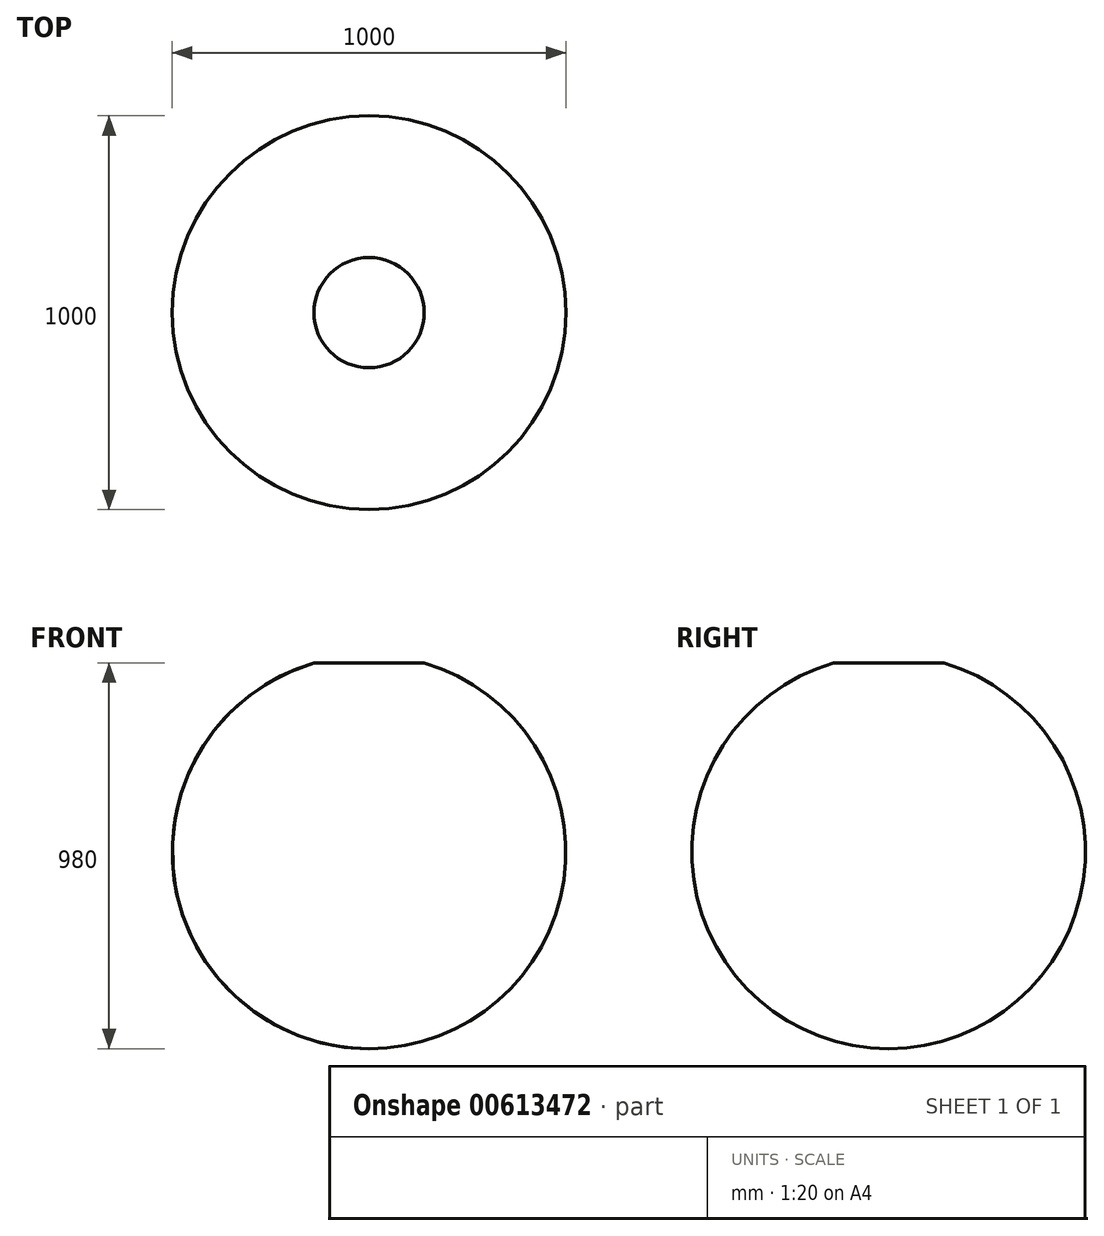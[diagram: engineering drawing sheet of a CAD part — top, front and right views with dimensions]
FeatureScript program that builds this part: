
annotation { "Feature Type Name" : "Feature", "Feature Type Description" : "" }
export const myFeature = defineFeature(function(context is Context, id is Id, definition is map)
    precondition{}
    {
        {
            var Q0;
            Q0=qCreatedBy(makeId("Front.planeOp"),FACE);
            var sketch = newSketch(context, id + "F0", { "sketchPlane" : qUnion([Q0])});
            skPoint(sketch, "E0", {"position": v(0, 0) * mm});
            skLineSegment(sketch, "E1", {"start": v(0, 480) * mm, "end": v(0, -500) * mm});
            skLineSegment(sketch, "E2", {"start": v(0, 480) * mm, "end": v(140, 480) * mm});
            skArc(sketch, "E3", {"start": v(140, 480) * mm, "mid": v(494.97, -70.71) * mm, "end": v(0, -500) * mm});
            skSolve(sketch);
        }
        {
            var Q0;
            Q0=makeQuery(id+"F0.imprint","IMPRINT",FACE,{"disambiguationData":[TD([[makeQuery(id+"F0.imprint","IMPRINT",EDGE,{"derivedFrom":sQuery(id+"F0.wireOp",EDGE,"E1")}),1.0]])]});
            var Q1;
            Q1=sQuery(id+"F0.wireOp",EDGE,"E3");
            var Q2;
            Q2=sQuery(id+"F0.wireOp",EDGE,"E1");
            revolve(context, id + "F1", {"bodyType" : ToolBodyType.SURFACE, "entities" : qUnion([Q0]), "surfaceEntities" : qUnion([Q1]), "axis" : qUnion([Q2]), "revolveType" : RevolveType.FULL});
        }
    });
